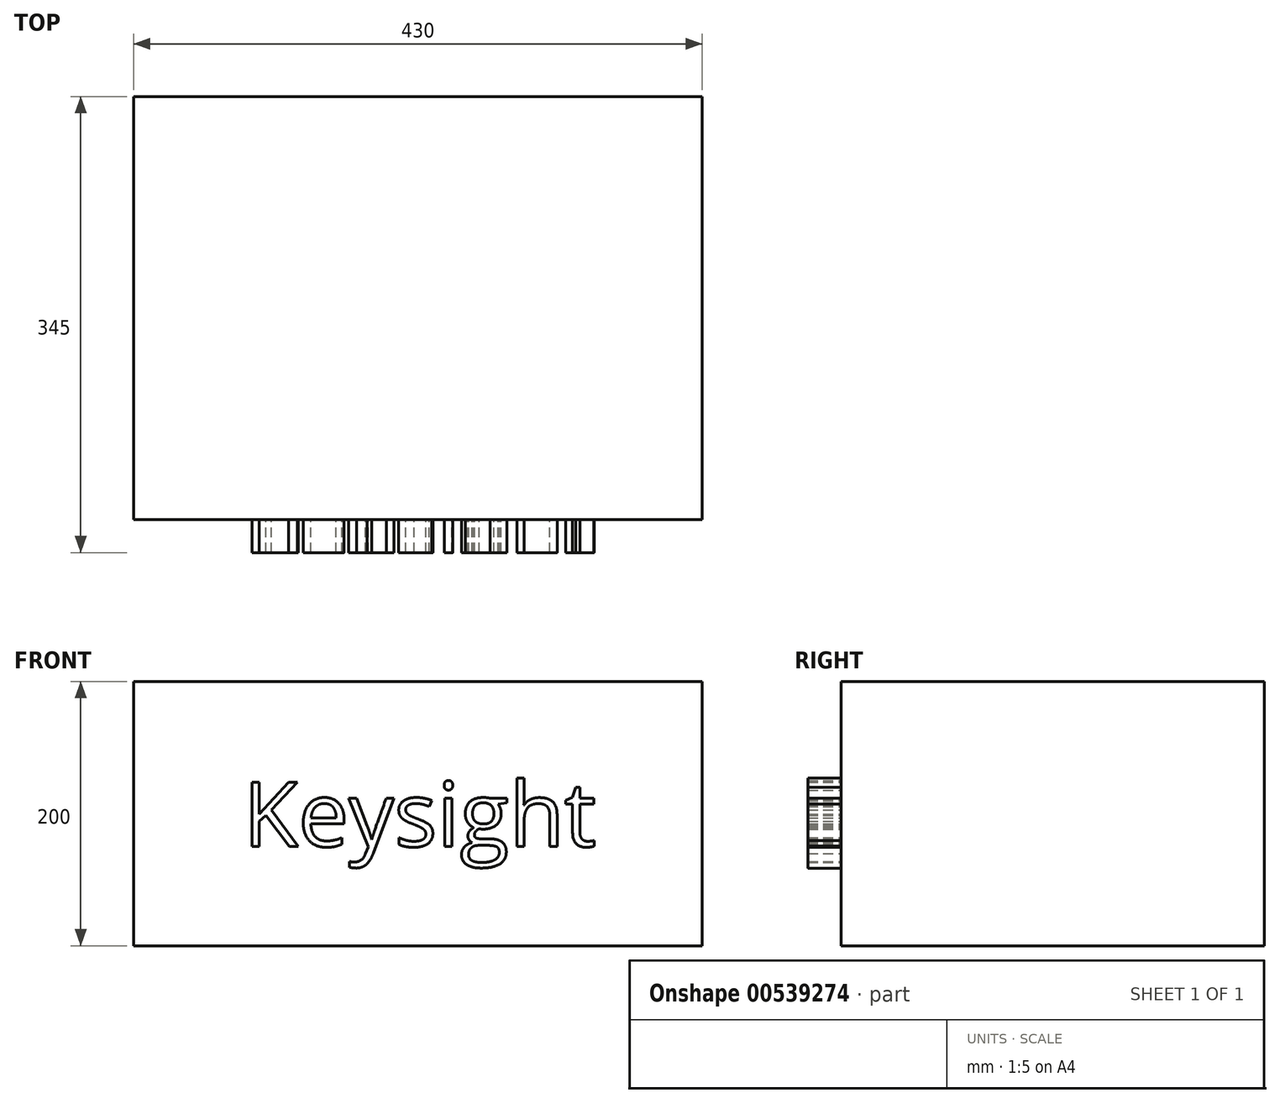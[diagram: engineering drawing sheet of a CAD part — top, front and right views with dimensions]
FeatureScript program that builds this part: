
annotation { "Feature Type Name" : "Feature", "Feature Type Description" : "" }
export const myFeature = defineFeature(function(context is Context, id is Id, definition is map)
    precondition{}
    {
        {
            var Q0;
            Q0=qCreatedBy(makeId("Front.planeOp"),FACE);
            var sketch = newSketch(context, id + "F0", { "sketchPlane" : qUnion([Q0])});
            skLineSegment(sketch, "E0.bottom", {"start": v(-215, -100) * mm, "end": v(215, -100) * mm});
            skLineSegment(sketch, "E0.top", {"start": v(-215, 100) * mm, "end": v(215, 100) * mm});
            skLineSegment(sketch, "E0.left", {"start": v(-215, -100) * mm, "end": v(-215, 100) * mm});
            skLineSegment(sketch, "E0.right", {"start": v(215, -100) * mm, "end": v(215, 100) * mm});
            skPoint(sketch, "E0.middle", {"position": v(0, 0) * mm});
            skSolve(sketch);
        }
        {
            var Q0;
            Q0=makeQuery(id+"F0.imprint","IMPRINT",FACE,{"disambiguationData":[TD([[makeQuery(id+"F0.imprint","IMPRINT",EDGE,{"derivedFrom":sQuery(id+"F0.wireOp",EDGE,"E0.bottom")}),1.0]])]});
            extrude(context, id + "F1", {"entities" : qUnion([Q0]), "depth" : 320 * mm, "offsetDistance" : 25 * mm});
        }
        {
            var Q0;
            Q0=makeQuery(id+"F1.opExtrude","CAP_FACE",FACE,{"disambiguationData":[OSD([sQuery(id+"F0.wireOp",EDGE,"E0.bottom"),sQuery(id+"F0.wireOp",EDGE,"E0.top"),sQuery(id+"F0.wireOp",EDGE,"E0.left"),sQuery(id+"F0.wireOp",EDGE,"E0.right")])],"isStart":false});
            var sketch = newSketch(context, id + "F2", { "sketchPlane" : qUnion([Q0])});
            skText(sketch, "E1", { "text": "Keysight", "fontName": "OpenSans-Regular.ttf"});
            const initialGuessF2  = {"E1": [-0.13228, -0.02488, 1, 0, 0.049]};
            skSetInitialGuess(sketch, initialGuessF2);
            skSolve(sketch);
        }
        {
            var Q0;
            Q0 = qSketchRegion(id + "F2", true);
            extrude(context, id + "F3", {"entities" : qUnion([Q0]), "operationType" : NewBodyOperationType.ADD, "depth" : 25 * mm, "offsetDistance" : 25 * mm});
        }
    });
